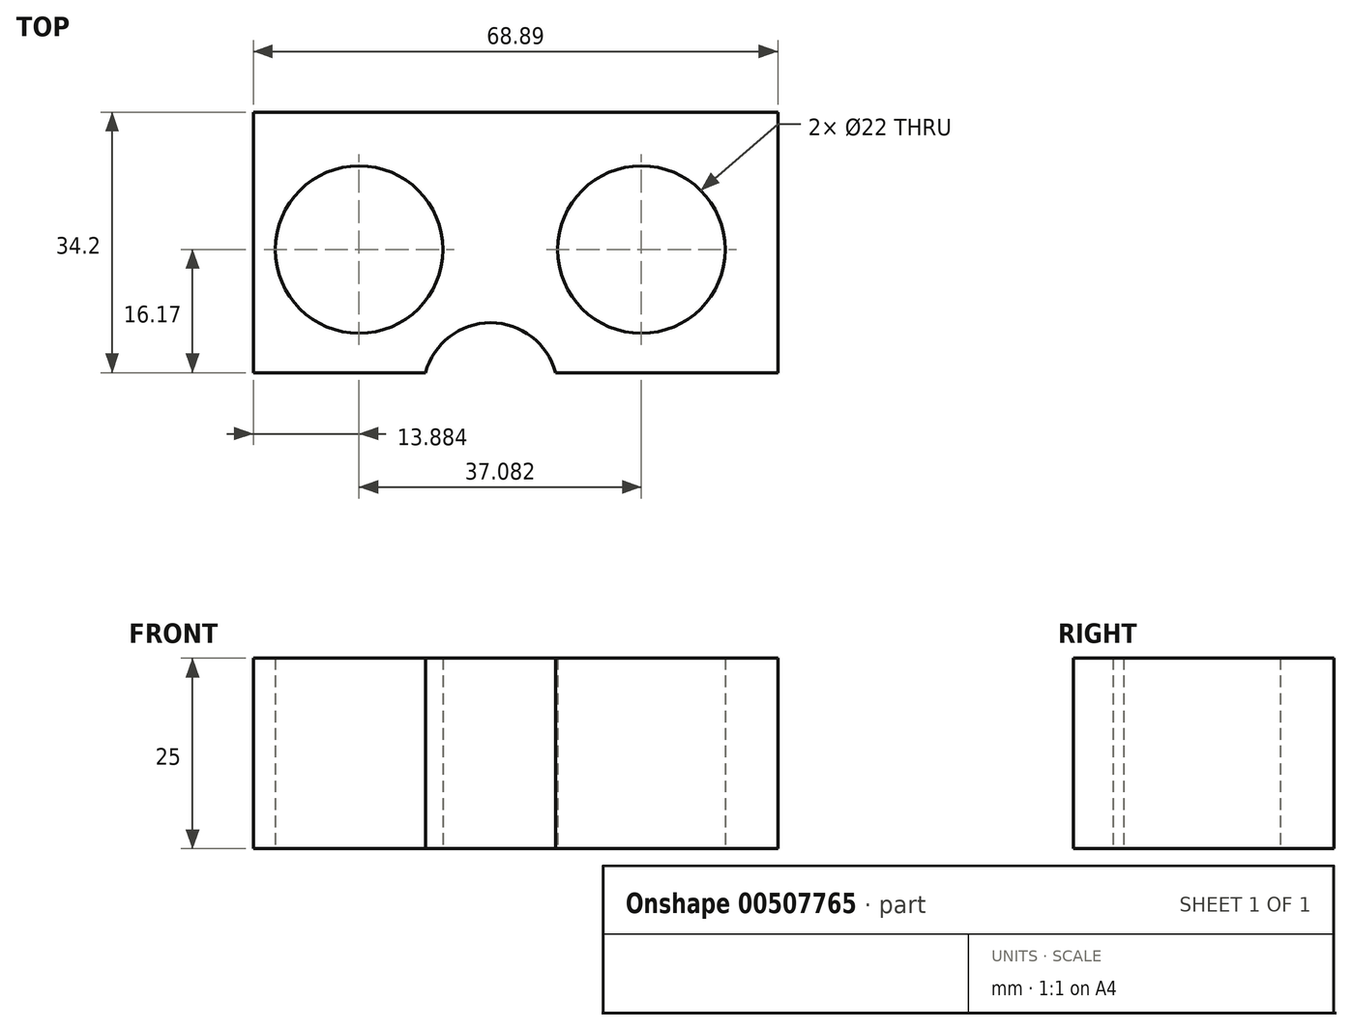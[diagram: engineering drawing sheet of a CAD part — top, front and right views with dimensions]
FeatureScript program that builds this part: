
annotation { "Feature Type Name" : "Feature", "Feature Type Description" : "" }
export const myFeature = defineFeature(function(context is Context, id is Id, definition is map)
    precondition{}
    {
        {
            var Q0;
            Q0=qCreatedBy(makeId("Top.planeOp"),FACE);
            var sketch = newSketch(context, id + "F0", { "sketchPlane" : qUnion([Q0])});
            skLineSegment(sketch, "E0.bottom", {"start": v(-37.95, -16.17) * mm, "end": v(30.94, -16.17) * mm});
            skLineSegment(sketch, "E0.top", {"start": v(-37.95, 18.03) * mm, "end": v(30.94, 18.03) * mm});
            skLineSegment(sketch, "E0.left", {"start": v(-37.95, -16.17) * mm, "end": v(-37.95, 18.03) * mm});
            skLineSegment(sketch, "E0.right", {"start": v(30.94, -16.17) * mm, "end": v(30.94, 18.03) * mm});
            skCircle(sketch, "E1", {"center": v(13.02, 0) * mm, "radius": 11 * mm});
            skCircle(sketch, "E2", {"center": v(-24.07, 0) * mm, "radius": 11 * mm});
            skSolve(sketch);
        }
        {
            var Q0;
            Q0=makeQuery(id+"F0.imprint","IMPRINT",FACE,{"disambiguationData":[TD([[makeQuery(id+"F0.imprint","IMPRINT",EDGE,{"derivedFrom":sQuery(id+"F0.wireOp",EDGE,"E0.bottom")}),1.0]])]});
            extrude(context, id + "F1", {"entities" : qUnion([Q0]), "depth" : 25 * mm, "offsetDistance" : 25 * mm});
        }
        {
            var Q0;
            Q0=makeQuery(id+"F1.opExtrude","CAP_FACE",FACE,{"disambiguationData":[OSD([sQuery(id+"F0.wireOp",EDGE,"E0.bottom"),sQuery(id+"F0.wireOp",EDGE,"E0.top"),sQuery(id+"F0.wireOp",EDGE,"E0.left"),sQuery(id+"F0.wireOp",EDGE,"E0.right"),sQuery(id+"F0.wireOp",EDGE,"E1"),sQuery(id+"F0.wireOp",EDGE,"E2")])],"isStart":true});
            var sketch = newSketch(context, id + "F2", { "sketchPlane" : qUnion([Q0])});
            skArc(sketch, "E3", {"start": v(-15.34, 16.17) * mm, "mid": v(-6.8, 9.6) * mm, "end": v(1.74, 16.17) * mm});
            skSolve(sketch);
        }
        {
            var Q0;
            Q0 = qSketchRegion(id + "F2", true);
            var Q1;
            {var subQ0=sQuery(id+"F2.wireOp",EDGE,"E3");Q1=makeQuery(id+"F2.imprint","IMPRINT",FACE,{"disambiguationData":[TD([[makeQuery(id+"F2.imprint","IMPRINT",EDGE,{"derivedFrom":subQ0}),1.0]])]});}
            extrude(context, id + "F3", {"entities" : qUnion([Q0, Q1]), "operationType" : NewBodyOperationType.REMOVE, "endBound" : BoundingType.THROUGH_ALL, "oppositeDirection" : true, "depth" : 25 * mm, "offsetDistance" : 25 * mm});
        }
    });
